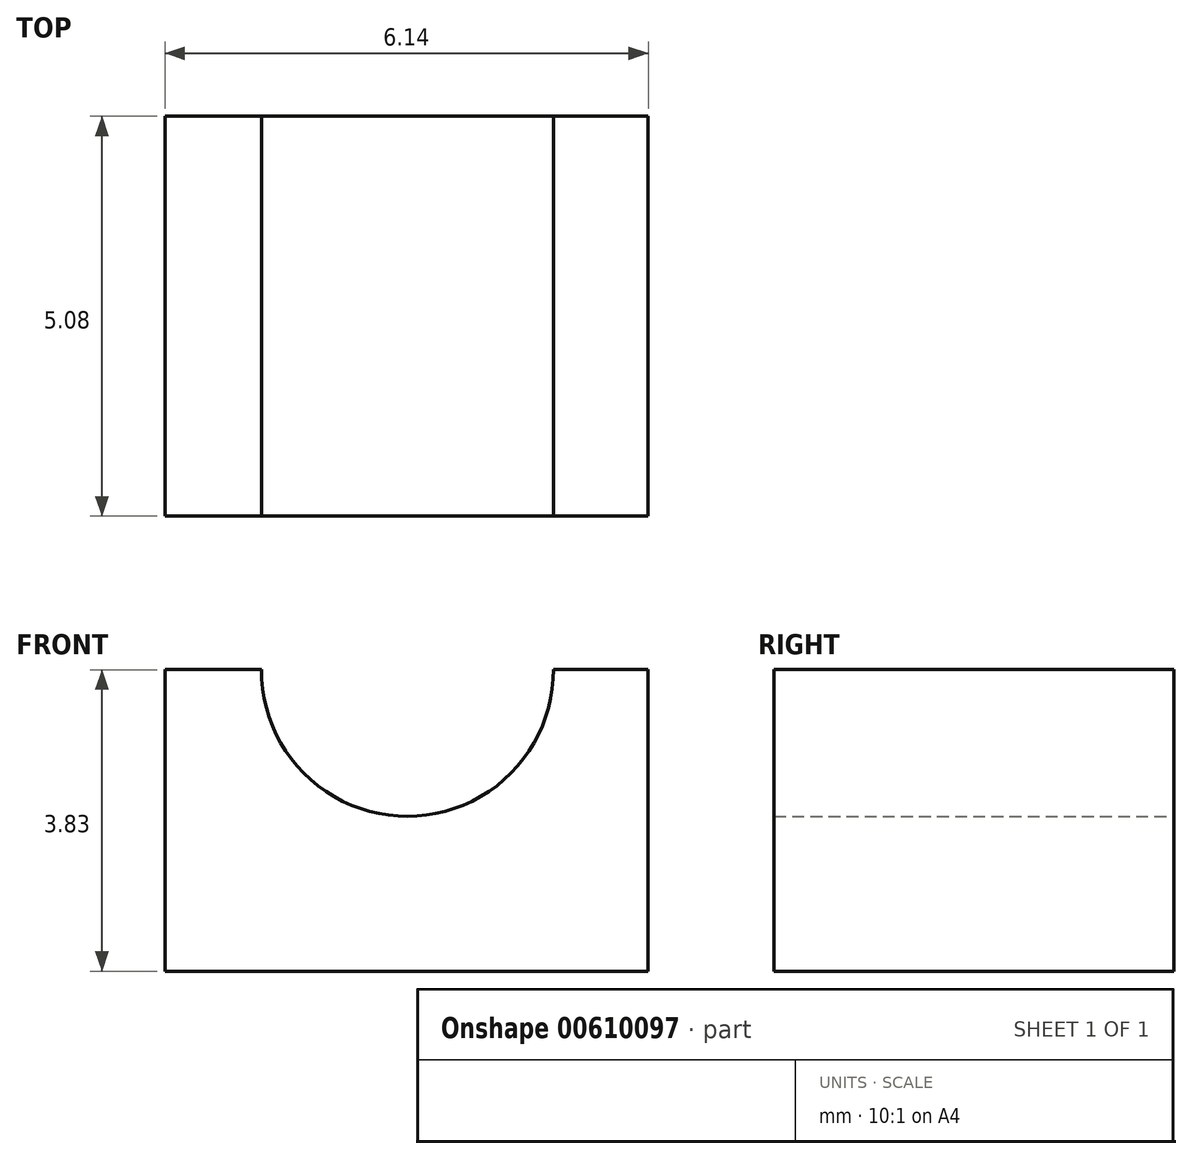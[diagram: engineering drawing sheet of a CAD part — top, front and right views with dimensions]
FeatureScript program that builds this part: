
annotation { "Feature Type Name" : "Feature", "Feature Type Description" : "" }
export const myFeature = defineFeature(function(context is Context, id is Id, definition is map)
    precondition{}
    {
        {
            var Q0;
            Q0=qCreatedBy(makeId("Front.planeOp"),FACE);
            var sketch = newSketch(context, id + "F0", { "sketchPlane" : qUnion([Q0])});
            skLineSegment(sketch, "E0", {"start": v(-58.4, -7.54) * mm, "end": v(-52.27, -7.54) * mm});
            skLineSegment(sketch, "E1", {"start": v(-58.4, -7.54) * mm, "end": v(-58.4, -3.7) * mm});
            skLineSegment(sketch, "E2", {"start": v(-58.4, -3.7) * mm, "end": v(-57.18, -3.7) * mm});
            skLineSegment(sketch, "E3", {"start": v(-52.27, -3.7) * mm, "end": v(-52.27, -7.54) * mm});
            skArc(sketch, "E4", {"start": v(-57.18, -3.7) * mm, "mid": v(-55.33, -5.57) * mm, "end": v(-53.48, -3.7) * mm});
            skLineSegment(sketch, "E5.trimOffspring", {"start": v(-53.48, -3.7) * mm, "end": v(-52.27, -3.7) * mm});
            skSolve(sketch);
        }
        {
            var Q0;
            Q0 = qSketchRegion(id + "F0", true);
            extrude(context, id + "F1", {"entities" : qUnion([Q0]), "depth" : 5.08 * mm, "offsetDistance" : 25.4 * mm});
        }
    });
